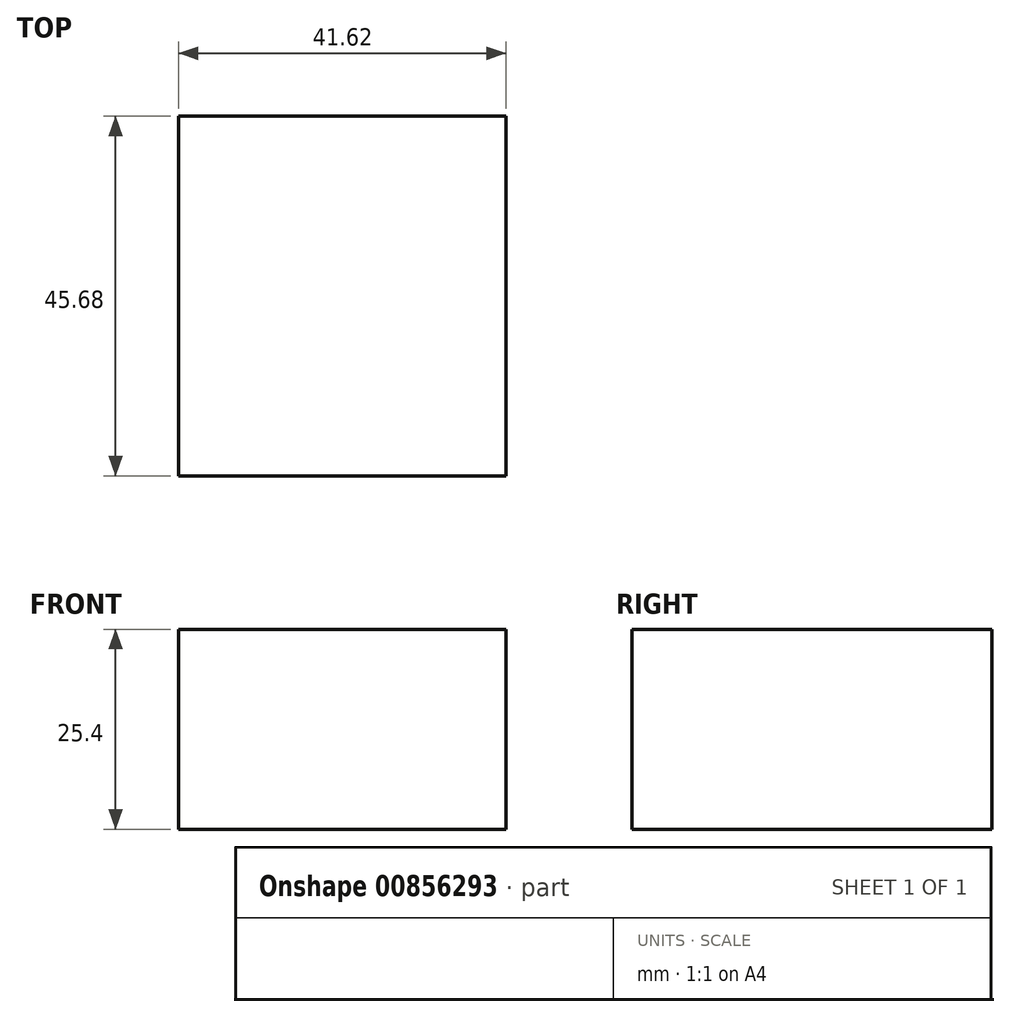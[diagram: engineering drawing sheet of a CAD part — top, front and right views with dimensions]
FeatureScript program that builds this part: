
annotation { "Feature Type Name" : "Feature", "Feature Type Description" : "" }
export const myFeature = defineFeature(function(context is Context, id is Id, definition is map)
    precondition{}
    {
        {
            var Q0;
            Q0=qCreatedBy(makeId("Top.planeOp"),FACE);
            var sketch = newSketch(context, id + "F0", { "sketchPlane" : qUnion([Q0])});
            skLineSegment(sketch, "E0", {"start": v(12.57, -45.68) * mm, "end": v(41.62, -45.68) * mm});
            skLineSegment(sketch, "E1", {"start": v(41.62, -45.68) * mm, "end": v(41.62, -11.25) * mm});
            skLineSegment(sketch, "E2", {"start": v(41.62, -11.25) * mm, "end": v(41.62, 0) * mm});
            skLineSegment(sketch, "E3", {"start": v(41.62, 0) * mm, "end": v(0, 0) * mm});
            skLineSegment(sketch, "E4", {"start": v(0, 0) * mm, "end": v(0, -45.68) * mm});
            skLineSegment(sketch, "E5", {"start": v(0, -45.68) * mm, "end": v(12.57, -45.68) * mm});
            skSolve(sketch);
        }
        {
            var Q0;
            Q0=makeQuery(id+"F0.imprint","IMPRINT",FACE,{"disambiguationData":[TD([[makeQuery(id+"F0.imprint","IMPRINT",EDGE,{"derivedFrom":sQuery(id+"F0.wireOp",EDGE,"E0")}),1.0]])]});
            extrude(context, id + "F1", {"entities" : qUnion([Q0]), "depth" : 25.4 * mm, "offsetDistance" : 25.4 * mm});
        }
    });
